# Revit family: BIMLIB_КарманныйФильтр_FBRr_SHUFT
name_source: partatom
category: Арматура воздуховодов
revit_build: Autodesk Revit 2017 (Build: 20170118_1100(x64)
units: mm (PartAtom-declared; Revit-internal decimal feet)

## family parameters
Всегда вертикально = Да
На основе рабочей плоскости = Нет
Общий = Нет
При загрузке вырезать с полостями = Нет
Размер круглого соединителя = Использовать диаметр
Тип детали = Вставляется

## types (1)
- BIMLIB_КарманныйФильтр_FBRr_SHUFT
    ADSK_URL документации изделия = http://www.shuft.ru
    ADSK_URL страницы изделия = http://www.shuft.ru
    ADSK_Версия Revit = 2017
    ADSK_Версия семейства = v.1
    ADSK_Единица измерения = шт.
    ADSK_Завод-изготовитель = ООО «Завод ВКО» марка SHUFT
    ADSK_Материал = BIMLIB_Сталь_SHUFT
    BL_BIM library = https://bimlib.pro
    URL = http://www.shuft.ru
    Изготовитель = ООО «Завод ВКО» марка SHUFT
    Описание = Воздушные фильтры cерии FBRr предназначены для очистки от пыли наружного и рециркуляционного воздуха в системах приточной вентиляции и кондиционирования.

Фильтруемый воздух не должен содержать агрессивных газов и паров. Допустимая температура перемещаемого воздуха от –40 до +70°С. Корпус фильтр-бокса FBRr выполнен из оцинкованной стали. Фильтрующие вставки FR к карманным фильтрам FBR изготавливаются из нетканого материала с классом очистки F3 (EU3), F5 (EU5), F5 (EU7). Для простоты обслуживания фильтрующие вставки устанавливаются в направляющих. Наличие фланцев с обеих сторон фильтра обеспечивает простоту монтажа. Фильтры FBR могут устанавливаться вертикально или горизонтально.
    Таблица = FBRr
